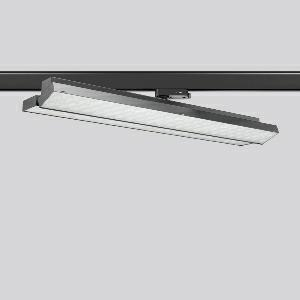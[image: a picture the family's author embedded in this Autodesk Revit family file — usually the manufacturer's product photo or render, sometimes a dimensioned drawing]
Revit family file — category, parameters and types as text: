
# Revit family: tx-move_742163_003_3_76_228d
name_source: partatom
category: Lighting Fixtures
units: mm (PartAtom-declared; Revit-internal decimal feet)

## family parameters
Cut with Voids When Loaded = No
Host = Face
Light Source = No
Part Type = Normal
Room Calculation Point = No
Round Connector Dimension = Use Diameter
Shared = No

## types (1)
- MultiLumen 1 (1 x LED Modul 835, 2875 lm, 3500)
    Apparent Load = 41 VA
    CIE Flux Codes = 65 90 98 100 100
    Color Rendering = 80
    Color Temperature = 3500
    Default Elevation = 1800 mm
    Description = Series: TX-MOVE
Multifunctional surface-mounted spotlight for area lighting. Very flat design. Housing: sheet steel, powder-coated. Rotation range: 356°. Swivel range: 90°. Consistent alignment possible with visible tilt scale. High-efficiency LED units with optimum light control thanks to clear plastic (PC) lens optics. Spezielle Mikrostrukturen reduzieren Gelbsaum. Asymmetrical light distribution. With adapter for RZB 3-circuit DALI tracks. Suitable for Track on ceiling. MultiLumen: Luminous flux adjustable in 3 steps. Factory setting is the highest luminous flux. Environmentally friendly and resource-saving due to replaceable and recyclable components. 
Colour: deep black, matt (RAL 9005)
Length: 570 mm
Width: 119 mm
Height: 88 mm
Lamp: LED
Socket: without socket
Colour temperature: 3500K
Colour rendering index (CRI): 80
System power: 41 W
Rated luminous flux: 5750 lm
Luminous efficiency: 140 lm/W
System power 2: 57 W
Rated luminous flux 2: 7750 lm
Luminous efficiency 2: 136 lm/W
System power 3: 73 W
Rated luminous flux 3: 9450 lm
Luminous efficiency 3: 129 lm/W
Control gear: Dimmable EVG, DALI
Protection class: I
Type of protection: IP 20
    Height = 75 mm
    Lamp = 1 x LED Modul 835
    Lamp Light Flux = 2875 lm
    Lamp count = 1
    Length = 569 mm
    Lifetime = 50000 h
    Luminous efficacy = 140 lm/W
    Manufacturer = RZB
    ModVariant = No
    Model = 742163.003.3.76
    Mounting Place = Ceiling
    Mounting Type = Rail mounted
    Number of Poles = 1
    OnlyDefault = Yes
    Power Factor = 1
    Product Name = TX-MOVE
    Product group = Track mounted projectors
    ProductGroupID = 301
    Protection Class = Protection class I
    Protection Degree = IP 20
    RLX_Detail_Level = 1
    RLX_Emergency_Light_Flux = 0 lm
    RLX_Emergency_Type = 0
    RLX_Emergency_Type_DB = No
    RlxData = <blob elided: 57405 chars, md5=dce078d8>
    Socket = socket
    Standby Power = 0 W
    System Light Flux = 5750 lm
    System Power = 41 W
    Type Comments = MultiLumen 1
    Type Image = 742162.003.jpg
    URL = http://relux.com
    VarID = multilumen_1
    Voltage = 230 V
    Voltage Range = 220-240 V
    Weight = 0.00 kg
    Width = 119 mm

## geometry (parser evidence)
native form markers: Blend x4, Sweep x14
no freeform markers — native parametric forms only
